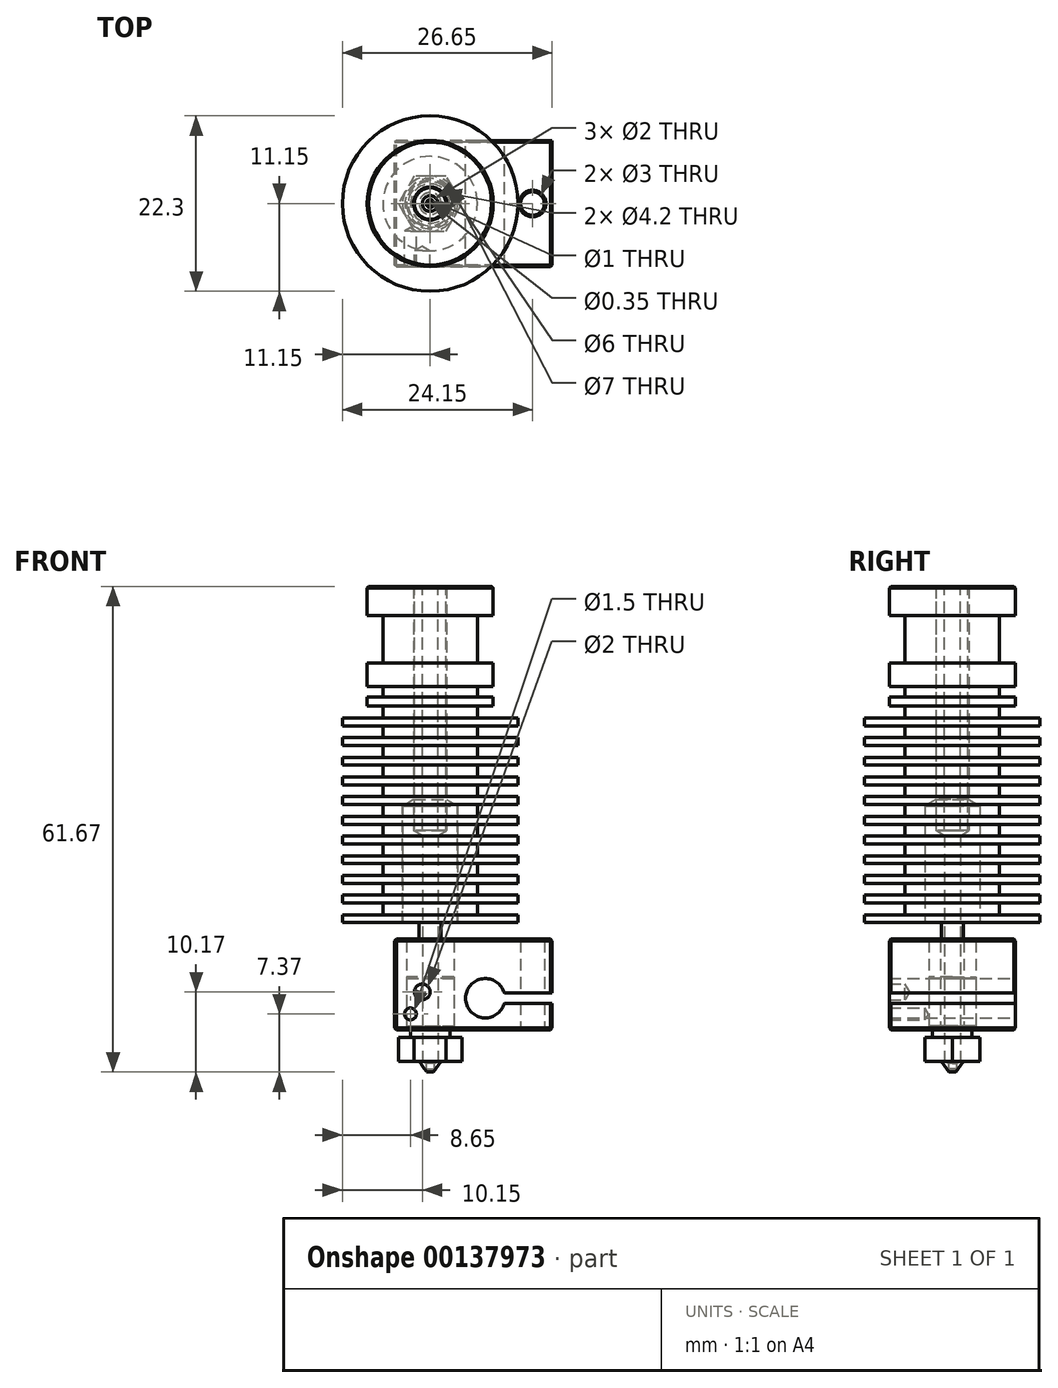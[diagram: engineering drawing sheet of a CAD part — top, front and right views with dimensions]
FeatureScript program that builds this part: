
annotation { "Feature Type Name" : "Feature", "Feature Type Description" : "" }
export const myFeature = defineFeature(function(context is Context, id is Id, definition is map)
    precondition{}
    {
        {
            assignVariable(context, id + "F0", {"name" : "A", "anyValue" : 0.35});
        }
        {
            assignVariable(context, id + "F1", {"name" : "D", "anyValue" : 1});
        }
        {
            var Q0;
            Q0=qCreatedBy(makeId("Front.planeOp"),FACE);
            var sketch = newSketch(context, id + "F2", { "sketchPlane" : qUnion([Q0])});
            skLineSegment(sketch, "E0", {"start": v(0, 21.35) * mm, "end": v(8, 21.35) * mm});
            skLineSegment(sketch, "E1", {"start": v(8, 21.35) * mm, "end": v(8, 17.65) * mm});
            skLineSegment(sketch, "E2", {"start": v(8, 17.65) * mm, "end": v(6, 17.65) * mm});
            skLineSegment(sketch, "E3", {"start": v(6, 17.65) * mm, "end": v(6, 11.65) * mm});
            skLineSegment(sketch, "E4", {"start": v(6, 11.65) * mm, "end": v(8, 11.65) * mm});
            skLineSegment(sketch, "E5", {"start": v(8, 11.65) * mm, "end": v(8, 8.65) * mm});
            skLineSegment(sketch, "E6", {"start": v(8, 8.65) * mm, "end": v(6, 8.65) * mm});
            skLineSegment(sketch, "E7", {"start": v(6, 8.65) * mm, "end": v(6, 7.3) * mm});
            skLineSegment(sketch, "E8", {"start": v(6, 7.3) * mm, "end": v(8, 7.3) * mm});
            skLineSegment(sketch, "E9", {"start": v(8, 7.3) * mm, "end": v(8, 6.15) * mm});
            skLineSegment(sketch, "E10", {"start": v(8, 6.15) * mm, "end": v(6, 6.15) * mm});
            skLineSegment(sketch, "E11", {"start": v(6, 6.15) * mm, "end": v(6, 4.65) * mm});
            skLineSegment(sketch, "E12", {"start": v(6, 4.65) * mm, "end": v(11.15, 4.65) * mm});
            skLineSegment(sketch, "E13", {"start": v(11.15, 4.65) * mm, "end": v(11.15, 3.65) * mm});
            skLineSegment(sketch, "E14", {"start": v(11.15, 3.65) * mm, "end": v(6, 3.65) * mm});
            skLineSegment(sketch, "E15.0.1.0", {"start": v(6, 3.65) * mm, "end": v(6, 2.15) * mm});
            skLineSegment(sketch, "E15.0.1.1", {"start": v(6, 2.15) * mm, "end": v(11.15, 2.15) * mm});
            skLineSegment(sketch, "E15.0.1.2", {"start": v(11.15, 2.15) * mm, "end": v(11.15, 1.15) * mm});
            skLineSegment(sketch, "E15.0.1.3", {"start": v(11.15, 1.15) * mm, "end": v(6, 1.15) * mm});
            skLineSegment(sketch, "E15.0.2.0", {"start": v(6, 1.15) * mm, "end": v(6, -0.35) * mm});
            skLineSegment(sketch, "E15.0.2.1", {"start": v(6, -0.35) * mm, "end": v(11.15, -0.35) * mm});
            skLineSegment(sketch, "E15.0.2.2", {"start": v(11.15, -0.35) * mm, "end": v(11.15, -1.35) * mm});
            skLineSegment(sketch, "E15.0.2.3", {"start": v(11.15, -1.35) * mm, "end": v(6, -1.35) * mm});
            skLineSegment(sketch, "E15.0.3.0", {"start": v(6, -1.35) * mm, "end": v(6, -2.85) * mm});
            skLineSegment(sketch, "E15.0.3.1", {"start": v(6, -2.85) * mm, "end": v(11.15, -2.85) * mm});
            skLineSegment(sketch, "E15.0.3.2", {"start": v(11.15, -2.85) * mm, "end": v(11.15, -3.85) * mm});
            skLineSegment(sketch, "E15.0.3.3", {"start": v(11.15, -3.85) * mm, "end": v(6, -3.85) * mm});
            skLineSegment(sketch, "E15.0.4.0", {"start": v(6, -3.85) * mm, "end": v(6, -5.35) * mm});
            skLineSegment(sketch, "E15.0.4.1", {"start": v(6, -5.35) * mm, "end": v(11.15, -5.35) * mm});
            skLineSegment(sketch, "E15.0.4.2", {"start": v(11.15, -5.35) * mm, "end": v(11.15, -6.35) * mm});
            skLineSegment(sketch, "E15.0.4.3", {"start": v(11.15, -6.35) * mm, "end": v(6, -6.35) * mm});
            skLineSegment(sketch, "E15.0.5.0", {"start": v(6, -6.35) * mm, "end": v(6, -7.85) * mm});
            skLineSegment(sketch, "E15.0.5.1", {"start": v(6, -7.85) * mm, "end": v(11.15, -7.85) * mm});
            skLineSegment(sketch, "E15.0.5.2", {"start": v(11.15, -7.85) * mm, "end": v(11.15, -8.85) * mm});
            skLineSegment(sketch, "E15.0.5.3", {"start": v(11.15, -8.85) * mm, "end": v(6, -8.85) * mm});
            skLineSegment(sketch, "E15.0.6.0", {"start": v(6, -8.85) * mm, "end": v(6, -10.35) * mm});
            skLineSegment(sketch, "E15.0.6.1", {"start": v(6, -10.35) * mm, "end": v(11.15, -10.35) * mm});
            skLineSegment(sketch, "E15.0.6.2", {"start": v(11.15, -10.35) * mm, "end": v(11.15, -11.35) * mm});
            skLineSegment(sketch, "E15.0.6.3", {"start": v(11.15, -11.35) * mm, "end": v(6, -11.35) * mm});
            skLineSegment(sketch, "E15.0.7.0", {"start": v(6, -11.35) * mm, "end": v(6, -12.85) * mm});
            skLineSegment(sketch, "E15.0.7.1", {"start": v(6, -12.85) * mm, "end": v(11.15, -12.85) * mm});
            skLineSegment(sketch, "E15.0.7.2", {"start": v(11.15, -12.85) * mm, "end": v(11.15, -13.85) * mm});
            skLineSegment(sketch, "E15.0.7.3", {"start": v(11.15, -13.85) * mm, "end": v(6, -13.85) * mm});
            skLineSegment(sketch, "E15.0.8.0", {"start": v(6, -13.85) * mm, "end": v(6, -15.35) * mm});
            skLineSegment(sketch, "E15.0.8.1", {"start": v(6, -15.35) * mm, "end": v(11.15, -15.35) * mm});
            skLineSegment(sketch, "E15.0.8.2", {"start": v(11.15, -15.35) * mm, "end": v(11.15, -16.35) * mm});
            skLineSegment(sketch, "E15.0.8.3", {"start": v(11.15, -16.35) * mm, "end": v(6, -16.35) * mm});
            skLineSegment(sketch, "E15.0.9.0", {"start": v(6, -16.35) * mm, "end": v(6, -17.85) * mm});
            skLineSegment(sketch, "E15.0.9.1", {"start": v(6, -17.85) * mm, "end": v(11.15, -17.85) * mm});
            skLineSegment(sketch, "E15.0.9.2", {"start": v(11.15, -17.85) * mm, "end": v(11.15, -18.85) * mm});
            skLineSegment(sketch, "E15.0.9.3", {"start": v(11.15, -18.85) * mm, "end": v(6, -18.85) * mm});
            skLineSegment(sketch, "E15.direction1", {"start": v(6, 3.65) * mm, "end": v(31, 3.65) * mm, "construction": true});
            skLineSegment(sketch, "E15.direction2", {"start": v(6, 3.65) * mm, "end": v(6, 1.15) * mm, "construction": true});
            skLineSegment(sketch, "E16", {"start": v(6, -18.85) * mm, "end": v(6, -20.35) * mm});
            skLineSegment(sketch, "E17", {"start": v(6, -20.35) * mm, "end": v(11.15, -20.35) * mm});
            skLineSegment(sketch, "E18", {"start": v(11.15, -20.35) * mm, "end": v(11.15, -21.35) * mm});
            skLineSegment(sketch, "E19", {"start": v(11.15, -21.35) * mm, "end": v(0, -21.35) * mm});
            skLineSegment(sketch, "E20", {"start": v(0, 21.35) * mm, "end": v(0, -21.35) * mm});
            skPoint(sketch, "E21.orphan", {"position": v(6, -21.35) * mm});
            skSolve(sketch);
        }
        {
            var Q0;
            Q0=makeQuery(id+"F2.imprint","IMPRINT",FACE,{"disambiguationData":[TD([[makeQuery(id+"F2.imprint","IMPRINT",EDGE,{"derivedFrom":sQuery(id+"F2.wireOp",EDGE,"E0")}),-1.0]])]});
            var Q1;
            Q1=sQuery(id+"F2.wireOp",EDGE,"E20");
            revolve(context, id + "F3", {"entities" : qUnion([Q0]), "axis" : qUnion([Q1]), "revolveType" : RevolveType.FULL});
        }
        {
            var Q0;
            Q0=makeQuery(id+"F3.opRevolve","SWEPT_FACE",FACE,{"disambiguationData":[OSD([sQuery(id+"F2.wireOp",EDGE,"E19")])]});
            var sketch = newSketch(context, id + "F4", { "sketchPlane" : qUnion([Q0])});
            skPoint(sketch, "E22", {"position": v(0, 0) * mm});
            skSolve(sketch);
        }
        {
            var Q0;
            Q0=sQuery(id+"F4.wireOp",VERTEX,"E22");
            var Q1;
            Q1=makeQuery(id+"F3.opRevolve","SWEPT_BODY",BODY,{"disambiguationData":[OSD([sQuery(id+"F2.wireOp",EDGE,"E0"),sQuery(id+"F2.wireOp",EDGE,"E1"),sQuery(id+"F2.wireOp",EDGE,"E2"),sQuery(id+"F2.wireOp",EDGE,"E3"),sQuery(id+"F2.wireOp",EDGE,"E4"),sQuery(id+"F2.wireOp",EDGE,"E5"),sQuery(id+"F2.wireOp",EDGE,"E6"),sQuery(id+"F2.wireOp",EDGE,"E7"),sQuery(id+"F2.wireOp",EDGE,"E8"),sQuery(id+"F2.wireOp",EDGE,"E9"),sQuery(id+"F2.wireOp",EDGE,"E10"),sQuery(id+"F2.wireOp",EDGE,"E11"),sQuery(id+"F2.wireOp",EDGE,"E12"),sQuery(id+"F2.wireOp",EDGE,"E13"),sQuery(id+"F2.wireOp",EDGE,"E14"),sQuery(id+"F2.wireOp",EDGE,"E15.0.1.0"),sQuery(id+"F2.wireOp",EDGE,"E15.0.1.1"),sQuery(id+"F2.wireOp",EDGE,"E15.0.1.2"),sQuery(id+"F2.wireOp",EDGE,"E15.0.1.3"),sQuery(id+"F2.wireOp",EDGE,"E15.0.2.0"),sQuery(id+"F2.wireOp",EDGE,"E15.0.2.1"),sQuery(id+"F2.wireOp",EDGE,"E15.0.2.2"),sQuery(id+"F2.wireOp",EDGE,"E15.0.2.3"),sQuery(id+"F2.wireOp",EDGE,"E15.0.3.0"),sQuery(id+"F2.wireOp",EDGE,"E15.0.3.1"),sQuery(id+"F2.wireOp",EDGE,"E15.0.3.2"),sQuery(id+"F2.wireOp",EDGE,"E15.0.3.3"),sQuery(id+"F2.wireOp",EDGE,"E15.0.4.0"),sQuery(id+"F2.wireOp",EDGE,"E15.0.4.1"),sQuery(id+"F2.wireOp",EDGE,"E15.0.4.2"),sQuery(id+"F2.wireOp",EDGE,"E15.0.4.3"),sQuery(id+"F2.wireOp",EDGE,"E15.0.5.0"),sQuery(id+"F2.wireOp",EDGE,"E15.0.5.1"),sQuery(id+"F2.wireOp",EDGE,"E15.0.5.2"),sQuery(id+"F2.wireOp",EDGE,"E15.0.5.3"),sQuery(id+"F2.wireOp",EDGE,"E15.0.6.0"),sQuery(id+"F2.wireOp",EDGE,"E15.0.6.1"),sQuery(id+"F2.wireOp",EDGE,"E15.0.6.2"),sQuery(id+"F2.wireOp",EDGE,"E15.0.6.3"),sQuery(id+"F2.wireOp",EDGE,"E15.0.7.0"),sQuery(id+"F2.wireOp",EDGE,"E15.0.7.1"),sQuery(id+"F2.wireOp",EDGE,"E15.0.7.2"),sQuery(id+"F2.wireOp",EDGE,"E15.0.7.3"),sQuery(id+"F2.wireOp",EDGE,"E15.0.8.0"),sQuery(id+"F2.wireOp",EDGE,"E15.0.8.1"),sQuery(id+"F2.wireOp",EDGE,"E15.0.8.2"),sQuery(id+"F2.wireOp",EDGE,"E15.0.8.3"),sQuery(id+"F2.wireOp",EDGE,"E15.0.9.0"),sQuery(id+"F2.wireOp",EDGE,"E15.0.9.1"),sQuery(id+"F2.wireOp",EDGE,"E15.0.9.2"),sQuery(id+"F2.wireOp",EDGE,"E15.0.9.3"),sQuery(id+"F2.wireOp",EDGE,"E16"),sQuery(id+"F2.wireOp",EDGE,"E17"),sQuery(id+"F2.wireOp",EDGE,"E18"),sQuery(id+"F2.wireOp",EDGE,"E19"),sQuery(id+"F2.wireOp",EDGE,"E20")])]});
            hole(context, id + "F5", {"style" : HoleStyle.SIMPLE, "endStyle" : HoleEndStyle.BLIND, "holeDiameter" : 7 * mm, "holeDepth" : 14.8 * mm, "locations" : qUnion([Q0]), "scope" : qUnion([Q1])});
        }
        {
            var Q0;
            Q0=qCreatedBy(makeId("Front.planeOp"),FACE);
            var sketch = newSketch(context, id + "F6", { "sketchPlane" : qUnion([Q0])});
            skLineSegment(sketch, "E23", {"start": v(0, -6.55) * mm, "end": v(3.5, -6.55) * mm});
            skLineSegment(sketch, "E24", {"start": v(3.5, -6.55) * mm, "end": v(3.5, -21.35) * mm});
            skLineSegment(sketch, "E25", {"start": v(3.5, -21.35) * mm, "end": v(1.4, -21.35) * mm});
            skLineSegment(sketch, "E26", {"start": v(1.4, -21.35) * mm, "end": v(1.4, -23.45) * mm});
            skLineSegment(sketch, "E27", {"start": v(1.4, -23.45) * mm, "end": v(3, -23.45) * mm});
            skLineSegment(sketch, "E28", {"start": v(3, -23.45) * mm, "end": v(3, -28.45) * mm});
            skLineSegment(sketch, "E29", {"start": v(3, -28.45) * mm, "end": v(0, -28.45) * mm});
            skLineSegment(sketch, "E30", {"start": v(0, -28.45) * mm, "end": v(0, -6.55) * mm});
            skLineSegment(sketch, "E31.0", {"start": v(3.5, -21.35) * mm, "end": v(-3.5, -21.35) * mm, "construction": true});
            skSolve(sketch);
        }
        {
            var Q0;
            Q0=qSketchRegion(id+"F6",true);
            var Q1;
            Q1=sQuery(id+"F6.wireOp",EDGE,"E30");
            revolve(context, id + "F7", {"entities" : qUnion([Q0]), "axis" : qUnion([Q1]), "revolveType" : RevolveType.FULL});
        }
        {
            var Q0;
            Q0=makeQuery(id+"F7.opRevolve","SWEPT_FACE",FACE,{"disambiguationData":[OSD([sQuery(id+"F6.wireOp",EDGE,"E23")])]});
            var sketch = newSketch(context, id + "F8", { "sketchPlane" : qUnion([Q0])});
            skPoint(sketch, "E32", {"position": v(0, 0) * mm});
            skSolve(sketch);
        }
        {
            var Q0;
            Q0=sQuery(id+"F8.wireOp",VERTEX,"E32");
            var Q1;
            Q1=makeQuery(id+"F7.opRevolve","SWEPT_BODY",BODY,{"disambiguationData":[OSD([sQuery(id+"F6.wireOp",EDGE,"E23"),sQuery(id+"F6.wireOp",EDGE,"E24"),sQuery(id+"F6.wireOp",EDGE,"E25"),sQuery(id+"F6.wireOp",EDGE,"E26"),sQuery(id+"F6.wireOp",EDGE,"E27"),sQuery(id+"F6.wireOp",EDGE,"E28"),sQuery(id+"F6.wireOp",EDGE,"E29"),sQuery(id+"F6.wireOp",EDGE,"E30")])]});
            hole(context, id + "F9", {"style" : HoleStyle.SIMPLE, "endStyle" : HoleEndStyle.THROUGH, "holeDiameter" : 2 * mm, "locations" : qUnion([Q0]), "scope" : qUnion([Q1]), "isTappedThrough" : true});
        }
        {
            var Q0;
            Q0=makeQuery(id+"F3.opRevolve","SWEPT_FACE",FACE,{"disambiguationData":[OSD([sQuery(id+"F2.wireOp",EDGE,"E0")])]});
            var sketch = newSketch(context, id + "F10", { "sketchPlane" : qUnion([Q0])});
            skPoint(sketch, "E33", {"position": v(0, 0) * mm});
            skSolve(sketch);
        }
        {
            var Q0;
            Q0=sQuery(id+"F10.wireOp",VERTEX,"E33");
            var Q1;
            Q1=makeQuery(id+"F3.opRevolve","SWEPT_BODY",BODY,{"disambiguationData":[OSD([sQuery(id+"F2.wireOp",EDGE,"E0"),sQuery(id+"F2.wireOp",EDGE,"E1"),sQuery(id+"F2.wireOp",EDGE,"E2"),sQuery(id+"F2.wireOp",EDGE,"E3"),sQuery(id+"F2.wireOp",EDGE,"E4"),sQuery(id+"F2.wireOp",EDGE,"E5"),sQuery(id+"F2.wireOp",EDGE,"E6"),sQuery(id+"F2.wireOp",EDGE,"E7"),sQuery(id+"F2.wireOp",EDGE,"E8"),sQuery(id+"F2.wireOp",EDGE,"E9"),sQuery(id+"F2.wireOp",EDGE,"E10"),sQuery(id+"F2.wireOp",EDGE,"E11"),sQuery(id+"F2.wireOp",EDGE,"E12"),sQuery(id+"F2.wireOp",EDGE,"E13"),sQuery(id+"F2.wireOp",EDGE,"E14"),sQuery(id+"F2.wireOp",EDGE,"E15.0.1.0"),sQuery(id+"F2.wireOp",EDGE,"E15.0.1.1"),sQuery(id+"F2.wireOp",EDGE,"E15.0.1.2"),sQuery(id+"F2.wireOp",EDGE,"E15.0.1.3"),sQuery(id+"F2.wireOp",EDGE,"E15.0.2.0"),sQuery(id+"F2.wireOp",EDGE,"E15.0.2.1"),sQuery(id+"F2.wireOp",EDGE,"E15.0.2.2"),sQuery(id+"F2.wireOp",EDGE,"E15.0.2.3"),sQuery(id+"F2.wireOp",EDGE,"E15.0.3.0"),sQuery(id+"F2.wireOp",EDGE,"E15.0.3.1"),sQuery(id+"F2.wireOp",EDGE,"E15.0.3.2"),sQuery(id+"F2.wireOp",EDGE,"E15.0.3.3"),sQuery(id+"F2.wireOp",EDGE,"E15.0.4.0"),sQuery(id+"F2.wireOp",EDGE,"E15.0.4.1"),sQuery(id+"F2.wireOp",EDGE,"E15.0.4.2"),sQuery(id+"F2.wireOp",EDGE,"E15.0.4.3"),sQuery(id+"F2.wireOp",EDGE,"E15.0.5.0"),sQuery(id+"F2.wireOp",EDGE,"E15.0.5.1"),sQuery(id+"F2.wireOp",EDGE,"E15.0.5.2"),sQuery(id+"F2.wireOp",EDGE,"E15.0.5.3"),sQuery(id+"F2.wireOp",EDGE,"E15.0.6.0"),sQuery(id+"F2.wireOp",EDGE,"E15.0.6.1"),sQuery(id+"F2.wireOp",EDGE,"E15.0.6.2"),sQuery(id+"F2.wireOp",EDGE,"E15.0.6.3"),sQuery(id+"F2.wireOp",EDGE,"E15.0.7.0"),sQuery(id+"F2.wireOp",EDGE,"E15.0.7.1"),sQuery(id+"F2.wireOp",EDGE,"E15.0.7.2"),sQuery(id+"F2.wireOp",EDGE,"E15.0.7.3"),sQuery(id+"F2.wireOp",EDGE,"E15.0.8.0"),sQuery(id+"F2.wireOp",EDGE,"E15.0.8.1"),sQuery(id+"F2.wireOp",EDGE,"E15.0.8.2"),sQuery(id+"F2.wireOp",EDGE,"E15.0.8.3"),sQuery(id+"F2.wireOp",EDGE,"E15.0.9.0"),sQuery(id+"F2.wireOp",EDGE,"E15.0.9.1"),sQuery(id+"F2.wireOp",EDGE,"E15.0.9.2"),sQuery(id+"F2.wireOp",EDGE,"E15.0.9.3"),sQuery(id+"F2.wireOp",EDGE,"E16"),sQuery(id+"F2.wireOp",EDGE,"E17"),sQuery(id+"F2.wireOp",EDGE,"E18"),sQuery(id+"F2.wireOp",EDGE,"E19"),sQuery(id+"F2.wireOp",EDGE,"E20")])]});
            var Q2;
            Q2=makeQuery(id+"F7.opRevolve","SWEPT_BODY",BODY,{"disambiguationData":[OSD([sQuery(id+"F6.wireOp",EDGE,"E23"),sQuery(id+"F6.wireOp",EDGE,"E24"),sQuery(id+"F6.wireOp",EDGE,"E25"),sQuery(id+"F6.wireOp",EDGE,"E26"),sQuery(id+"F6.wireOp",EDGE,"E27"),sQuery(id+"F6.wireOp",EDGE,"E28"),sQuery(id+"F6.wireOp",EDGE,"E29"),sQuery(id+"F6.wireOp",EDGE,"E30")])]});
            hole(context, id + "F11", {"style" : HoleStyle.SIMPLE, "endStyle" : HoleEndStyle.BLIND, "holeDiameter" : 4.2 * mm, "holeDepth" : 31 * mm, "locations" : qUnion([Q0]), "scope" : qUnion([Q1, Q2])});
        }
        {
            var Q0;
            Q0=qCreatedBy(makeId("Front.planeOp"),FACE);
            var sketch = newSketch(context, id + "F12", { "sketchPlane" : qUnion([Q0])});
            skLineSegment(sketch, "E34.0", {"start": v(-2.1, -9.65) * mm, "end": v(2.1, -9.65) * mm, "construction": true});
            skLineSegment(sketch, "E35.bottom", {"start": v(1, 21.35) * mm, "end": v(2, 21.35) * mm});
            skLineSegment(sketch, "E35.top", {"start": v(1, -9.65) * mm, "end": v(2, -9.65) * mm});
            skLineSegment(sketch, "E35.left", {"start": v(1, 21.35) * mm, "end": v(1, -9.65) * mm});
            skLineSegment(sketch, "E35.right", {"start": v(2, 21.35) * mm, "end": v(2, -9.65) * mm});
            skLineSegment(sketch, "E36", {"start": v(0, 26.07) * mm, "end": v(0, -35.6) * mm, "construction": true});
            skLineSegment(sketch, "E37.0", {"start": v(-2.1, 21.35) * mm, "end": v(2.1, 21.35) * mm, "construction": true});
            skSolve(sketch);
        }
        {
            var Q0;
            Q0=qSketchRegion(id+"F12",true);
            var Q1;
            Q1=qConstructionFilter(qBodyType(qCreatedBy(id+"F12",EDGE),BodyType.WIRE),ConstructionObject.NO);
            var Q2;
            Q2=sQuery(id+"F12.wireOp",EDGE,"E36");
            revolve(context, id + "F13", {"entities" : qUnion([Q0]), "surfaceEntities" : qUnion([Q1]), "axis" : qUnion([Q2]), "revolveType" : RevolveType.FULL});
        }
        {
            var Q0;
            Q0=makeQuery(id+"F7.opRevolve","SWEPT_FACE",FACE,{"disambiguationData":[OSD([sQuery(id+"F6.wireOp",EDGE,"E27")])]});
            var sketch = newSketch(context, id + "F14", { "sketchPlane" : qUnion([Q0])});
            skLineSegment(sketch, "E38.bottom", {"start": v(-4.5, -8) * mm, "end": v(15.5, -8) * mm});
            skLineSegment(sketch, "E38.top", {"start": v(-4.5, 8) * mm, "end": v(15.5, 8) * mm});
            skLineSegment(sketch, "E38.left", {"start": v(-4.5, -8) * mm, "end": v(-4.5, 8) * mm});
            skLineSegment(sketch, "E38.right", {"start": v(15.5, -8) * mm, "end": v(15.5, 8) * mm});
            skPoint(sketch, "E39", {"position": v(0, 0) * mm});
            skPoint(sketch, "E40", {"position": v(13, 0) * mm});
            skSolve(sketch);
        }
        {
            var Q0;
            Q0=qSketchRegion(id+"F14",true);
            extrude(context, id + "F15", {"entities" : qUnion([Q0]), "oppositeDirection" : true, "depth" : 11.5 * mm});
        }
        {
            var Q0;
            Q0=sQuery(id+"F14.wireOp",VERTEX,"E39");
            var Q1;
            Q1=makeQuery(id+"F15.opExtrude","SWEPT_BODY",BODY,{"disambiguationData":[OSD([sQuery(id+"F14.wireOp",EDGE,"E38.bottom"),sQuery(id+"F14.wireOp",EDGE,"E38.top"),sQuery(id+"F14.wireOp",EDGE,"E38.left"),sQuery(id+"F14.wireOp",EDGE,"E38.right")])]});
            hole(context, id + "F16", {"style" : HoleStyle.SIMPLE, "endStyle" : HoleEndStyle.THROUGH, "holeDiameter" : 6 * mm, "locations" : qUnion([Q0]), "scope" : qUnion([Q1]), "isTappedThrough" : true});
        }
        {
            var Q0;
            Q0=sQuery(id+"F14.wireOp",VERTEX,"E40");
            var Q1;
            Q1=makeQuery(id+"F15.opExtrude","SWEPT_BODY",BODY,{"disambiguationData":[OSD([sQuery(id+"F14.wireOp",EDGE,"E38.bottom"),sQuery(id+"F14.wireOp",EDGE,"E38.top"),sQuery(id+"F14.wireOp",EDGE,"E38.left"),sQuery(id+"F14.wireOp",EDGE,"E38.right")])]});
            hole(context, id + "F17", {"style" : HoleStyle.SIMPLE, "endStyle" : HoleEndStyle.THROUGH, "holeDiameter" : 3 * mm, "locations" : qUnion([Q0]), "scope" : qUnion([Q1]), "isTappedThrough" : true});
        }
        {
            var Q0;
            Q0=makeQuery(id+"F15.opExtrude","SWEPT_FACE",FACE,{"disambiguationData":[OSD([sQuery(id+"F14.wireOp",EDGE,"E38.bottom")])]});
            var sketch = newSketch(context, id + "F18", { "sketchPlane" : qUnion([Q0])});
            skPoint(sketch, "E41", {"position": v(-1, -30.15) * mm});
            skPoint(sketch, "E42", {"position": v(-2.5, -32.95) * mm});
            skPoint(sketch, "E43", {"position": v(7, -30.95) * mm});
            skLineSegment(sketch, "E44.bottom", {"start": v(15.5, -30.3) * mm, "end": v(7, -30.3) * mm});
            skLineSegment(sketch, "E44.top", {"start": v(15.5, -31.6) * mm, "end": v(7, -31.6) * mm});
            skLineSegment(sketch, "E44.left", {"start": v(15.5, -30.3) * mm, "end": v(15.5, -31.6) * mm});
            skLineSegment(sketch, "E44.right", {"start": v(7, -30.3) * mm, "end": v(7, -31.6) * mm});
            skSolve(sketch);
        }
        {
            var Q0;
            Q0=sQuery(id+"F18.wireOp",VERTEX,"E42");
            var Q1;
            Q1=makeQuery(id+"F15.opExtrude","SWEPT_BODY",BODY,{"disambiguationData":[OSD([sQuery(id+"F14.wireOp",EDGE,"E38.bottom"),sQuery(id+"F14.wireOp",EDGE,"E38.top"),sQuery(id+"F14.wireOp",EDGE,"E38.left"),sQuery(id+"F14.wireOp",EDGE,"E38.right")])]});
            hole(context, id + "F19", {"style" : HoleStyle.SIMPLE, "endStyle" : HoleEndStyle.BLIND, "holeDiameter" : 1.5 * mm, "holeDepth" : 4.5 * mm, "locations" : qUnion([Q0]), "scope" : qUnion([Q1])});
        }
        {
            var Q0;
            Q0=sQuery(id+"F18.wireOp",VERTEX,"E41");
            var Q1;
            Q1=makeQuery(id+"F15.opExtrude","SWEPT_BODY",BODY,{"disambiguationData":[OSD([sQuery(id+"F14.wireOp",EDGE,"E38.bottom"),sQuery(id+"F14.wireOp",EDGE,"E38.top"),sQuery(id+"F14.wireOp",EDGE,"E38.left"),sQuery(id+"F14.wireOp",EDGE,"E38.right")])]});
            hole(context, id + "F20", {"style" : HoleStyle.SIMPLE, "endStyle" : HoleEndStyle.BLIND, "holeDiameter" : 2 * mm, "holeDepth" : 2 * mm, "locations" : qUnion([Q0]), "scope" : qUnion([Q1])});
        }
        {
            var Q0;
            Q0=sQuery(id+"F18.wireOp",VERTEX,"E43");
            var Q1;
            Q1=makeQuery(id+"F15.opExtrude","SWEPT_BODY",BODY,{"disambiguationData":[OSD([sQuery(id+"F14.wireOp",EDGE,"E38.bottom"),sQuery(id+"F14.wireOp",EDGE,"E38.top"),sQuery(id+"F14.wireOp",EDGE,"E38.left"),sQuery(id+"F14.wireOp",EDGE,"E38.right")])]});
            hole(context, id + "F21", {"style" : HoleStyle.SIMPLE, "endStyle" : HoleEndStyle.THROUGH, "holeDiameter" : 5 * mm, "locations" : qUnion([Q0]), "scope" : qUnion([Q1]), "isTappedThrough" : true});
        }
        {
            var Q0;
            Q0=makeQuery(id+"F18.imprint","IMPRINT",FACE,{"disambiguationData":[TD([[makeQuery(id+"F18.imprint","IMPRINT",EDGE,{"derivedFrom":sQuery(id+"F18.wireOp",EDGE,"E44.bottom")}),1.0]])]});
            var Q1;
            Q1=makeQuery(id+"F15.opExtrude","SWEPT_BODY",BODY,{"disambiguationData":[OSD([sQuery(id+"F14.wireOp",EDGE,"E38.bottom"),sQuery(id+"F14.wireOp",EDGE,"E38.top"),sQuery(id+"F14.wireOp",EDGE,"E38.left"),sQuery(id+"F14.wireOp",EDGE,"E38.right")])]});
            extrude(context, id + "F22", {"entities" : qUnion([Q0]), "operationType" : NewBodyOperationType.REMOVE, "endBound" : BoundingType.UP_TO_BODY, "oppositeDirection" : true, "endBoundEntityBody" : qUnion([Q1]), "depth" : 25 * mm});
        }
        {
            var Q0;
            Q0=makeQuery(id+"F3.opRevolve","SWEPT_EDGE",EDGE,{"disambiguationData":[OSD([sQuery(id+"F2.wireOp",EDGE,"E0"),sQuery(id+"F2.wireOp",EDGE,"E1")])]});
            var Q1;
            Q1=makeQuery(id+"F5.hole-0.boolean.opBoolean","COPY",EDGE,{"derivedFrom":makeQuery(id+"F5.hole-0.opRevolve","SWEPT_EDGE",EDGE,{"disambiguationData":[OSD([sQuery(id+"F5.hole-0.sketch.wireOp",EDGE,"core_line_2"),sQuery(id+"F5.hole-0.sketch.wireOp",EDGE,"core_line_3")])]})});
            var Q2;
            Q2=makeQuery(id+"F5.hole-0.boolean.opBoolean","COPY",EDGE,{"derivedFrom":makeQuery(id+"F5.hole-0.opRevolve","SWEPT_EDGE",EDGE,{"disambiguationData":[OSD([sQuery(id+"F5.hole-0.sketch.wireOp",EDGE,"core_line_1"),sQuery(id+"F5.hole-0.sketch.wireOp",EDGE,"core_line_2")])]})});
            var Q3;
            Q3=makeQuery(id+"F7.opRevolve","SWEPT_EDGE",EDGE,{"disambiguationData":[OSD([sQuery(id+"F6.wireOp",EDGE,"E27"),sQuery(id+"F6.wireOp",EDGE,"E28")])]});
            var Q4;
            Q4=makeQuery(id+"F7.opRevolve","SWEPT_EDGE",EDGE,{"disambiguationData":[OSD([sQuery(id+"F6.wireOp",EDGE,"E28"),sQuery(id+"F6.wireOp",EDGE,"E29")])]});
            var Q5;
            Q5=makeQuery(id+"F9.hole-0.boolean.opBoolean","INTERSECT",EDGE,{"derivedFrom":[makeQuery(id+"F7.opRevolve","SWEPT_FACE",FACE,{"disambiguationData":[OSD([sQuery(id+"F6.wireOp",EDGE,"E29")])]}),makeQuery(id+"F9.hole-0.opRevolve","SWEPT_FACE",FACE,{"disambiguationData":[OSD([sQuery(id+"F9.hole-0.sketch.wireOp",EDGE,"core_line_2")])]})]});
            var Q6;
            Q6=makeQuery(id+"F15.opExtrude","CAP_EDGE",EDGE,{"disambiguationData":[OSD([sQuery(id+"F14.wireOp",EDGE,"E38.left")])],"isStart":true});
            var Q7;
            Q7=makeQuery(id+"F15.opExtrude","CAP_EDGE",EDGE,{"disambiguationData":[OSD([sQuery(id+"F14.wireOp",EDGE,"E38.bottom")])],"isStart":true});
            var Q8;
            Q8=makeQuery(id+"F15.opExtrude","SWEPT_EDGE",EDGE,{"disambiguationData":[OSD([sQuery(id+"F14.wireOp",EDGE,"E38.bottom"),sQuery(id+"F14.wireOp",EDGE,"E38.left")])]});
            var Q9;
            {var subQ0=sQuery(id+"F14.wireOp",EDGE,"E38.bottom");var subQ1=sQuery(id+"F14.wireOp",EDGE,"E38.right");Q9=makeQuery(id+"F22.boolean.opBoolean","SPLIT",EDGE,{"disambiguationData":[TD([makeQuery(id+"F22.opExtrude","SWEPT_FACE",FACE,{"disambiguationData":[OSD([sQuery(id+"F18.wireOp",EDGE,"E44.bottom")])]})])],"derivedFrom":makeQuery(id+"F15.opExtrude","SWEPT_EDGE",EDGE,{"disambiguationData":[OSD([subQ0,subQ1])]})});}
            var Q10;
            {var subQ0=sQuery(id+"F14.wireOp",EDGE,"E38.right");var subQ1=sQuery(id+"F14.wireOp",EDGE,"E38.top");Q10=makeQuery(id+"F22.boolean.opBoolean","SPLIT",EDGE,{"disambiguationData":[TD([makeQuery(id+"F22.opExtrude","SWEPT_FACE",FACE,{"disambiguationData":[OSD([sQuery(id+"F18.wireOp",EDGE,"E44.bottom")])]})])],"derivedFrom":makeQuery(id+"F15.opExtrude","SWEPT_EDGE",EDGE,{"disambiguationData":[OSD([subQ1,subQ0])]})});}
            var Q11;
            Q11=makeQuery(id+"F15.opExtrude","CAP_EDGE",EDGE,{"disambiguationData":[OSD([sQuery(id+"F14.wireOp",EDGE,"E38.top")])],"isStart":true});
            var Q12;
            Q12=makeQuery(id+"F15.opExtrude","CAP_EDGE",EDGE,{"disambiguationData":[OSD([sQuery(id+"F14.wireOp",EDGE,"E38.right")])],"isStart":true});
            var Q13;
            Q13=makeQuery(id+"F15.opExtrude","CAP_EDGE",EDGE,{"disambiguationData":[OSD([sQuery(id+"F14.wireOp",EDGE,"E38.right")])],"isStart":false});
            var Q14;
            {var subQ0=sQuery(id+"F14.wireOp",EDGE,"E38.bottom");var subQ1=sQuery(id+"F14.wireOp",EDGE,"E38.right");Q14=makeQuery(id+"F22.boolean.opBoolean","SPLIT",EDGE,{"disambiguationData":[TD([makeQuery(id+"F22.opExtrude","SWEPT_FACE",FACE,{"disambiguationData":[OSD([sQuery(id+"F18.wireOp",EDGE,"E44.top")])]})])],"derivedFrom":makeQuery(id+"F15.opExtrude","SWEPT_EDGE",EDGE,{"disambiguationData":[OSD([subQ0,subQ1])]})});}
            var Q15;
            Q15=makeQuery(id+"F15.opExtrude","CAP_EDGE",EDGE,{"disambiguationData":[OSD([sQuery(id+"F14.wireOp",EDGE,"E38.bottom")])],"isStart":false});
            var Q16;
            Q16=makeQuery(id+"F15.opExtrude","SWEPT_EDGE",EDGE,{"disambiguationData":[OSD([sQuery(id+"F14.wireOp",EDGE,"E38.top"),sQuery(id+"F14.wireOp",EDGE,"E38.left")])]});
            var Q17;
            Q17=makeQuery(id+"F15.opExtrude","CAP_EDGE",EDGE,{"disambiguationData":[OSD([sQuery(id+"F14.wireOp",EDGE,"E38.top")])],"isStart":false});
            var Q18;
            Q18=makeQuery(id+"F15.opExtrude","CAP_EDGE",EDGE,{"disambiguationData":[OSD([sQuery(id+"F14.wireOp",EDGE,"E38.left")])],"isStart":false});
            var Q19;
            Q19=makeQuery(id+"F19.hole-0.boolean.opBoolean","COPY",EDGE,{"derivedFrom":makeQuery(id+"F19.hole-0.opRevolve","SWEPT_EDGE",EDGE,{"disambiguationData":[OSD([sQuery(id+"F19.hole-0.sketch.wireOp",EDGE,"core_line_2"),sQuery(id+"F19.hole-0.sketch.wireOp",EDGE,"core_line_3")])]})});
            var Q20;
            Q20=makeQuery(id+"F20.hole-0.boolean.opBoolean","COPY",FACE,{"derivedFrom":makeQuery(id+"F20.hole-0.opRevolve","SWEPT_FACE",FACE,{"disambiguationData":[OSD([sQuery(id+"F20.hole-0.sketch.wireOp",EDGE,"core_line_2")])]})});
            var Q21;
            Q21=makeQuery(id+"F21.hole-0.boolean.opBoolean","COPY",EDGE,{"derivedFrom":makeQuery(id+"F21.hole-0.opRevolve","SWEPT_EDGE",EDGE,{"disambiguationData":[OSD([sQuery(id+"F21.hole-0.sketch.wireOp",EDGE,"core_line_2"),sQuery(id+"F21.hole-0.sketch.wireOp",EDGE,"core_line_3")])]})});
            var Q22;
            Q22=makeQuery(id+"F17.hole-0.boolean.opBoolean","COPY",EDGE,{"derivedFrom":makeQuery(id+"F17.hole-0.opRevolve","SWEPT_EDGE",EDGE,{"disambiguationData":[OSD([sQuery(id+"F17.hole-0.sketch.wireOp",EDGE,"core_line_2"),sQuery(id+"F17.hole-0.sketch.wireOp",EDGE,"core_line_3")])]})});
            var Q23;
            Q23=makeQuery(id+"F15.opExtrude","CAP_FACE",FACE,{"disambiguationData":[OSD([sQuery(id+"F14.wireOp",EDGE,"E38.bottom"),sQuery(id+"F14.wireOp",EDGE,"E38.top"),sQuery(id+"F14.wireOp",EDGE,"E38.left"),sQuery(id+"F14.wireOp",EDGE,"E38.right")])],"isStart":true});
            var Q24;
            Q24=makeQuery(id+"F21.hole-0.boolean.opBoolean","INTERSECT",EDGE,{"derivedFrom":[makeQuery(id+"F15.opExtrude","SWEPT_FACE",FACE,{"disambiguationData":[OSD([sQuery(id+"F14.wireOp",EDGE,"E38.top")])]}),makeQuery(id+"F21.hole-0.opRevolve","SWEPT_FACE",FACE,{"disambiguationData":[OSD([sQuery(id+"F21.hole-0.sketch.wireOp",EDGE,"core_line_2")])]})]});
            var Q25;
            Q25=makeQuery(id+"F17.hole-0.boolean.opBoolean","INTERSECT",EDGE,{"derivedFrom":[makeQuery(id+"F15.opExtrude","CAP_FACE",FACE,{"disambiguationData":[OSD([sQuery(id+"F14.wireOp",EDGE,"E38.bottom"),sQuery(id+"F14.wireOp",EDGE,"E38.top"),sQuery(id+"F14.wireOp",EDGE,"E38.left"),sQuery(id+"F14.wireOp",EDGE,"E38.right")])],"isStart":false}),makeQuery(id+"F17.hole-0.opRevolve","SWEPT_FACE",FACE,{"disambiguationData":[OSD([sQuery(id+"F17.hole-0.sketch.wireOp",EDGE,"core_line_2")])]})]});
            var Q26;
            Q26=makeQuery(id+"F16.hole-0.boolean.opBoolean","INTERSECT",EDGE,{"derivedFrom":[makeQuery(id+"F15.opExtrude","CAP_FACE",FACE,{"disambiguationData":[OSD([sQuery(id+"F14.wireOp",EDGE,"E38.bottom"),sQuery(id+"F14.wireOp",EDGE,"E38.top"),sQuery(id+"F14.wireOp",EDGE,"E38.left"),sQuery(id+"F14.wireOp",EDGE,"E38.right")])],"isStart":false}),makeQuery(id+"F16.hole-0.opRevolve","SWEPT_FACE",FACE,{"disambiguationData":[OSD([sQuery(id+"F16.hole-0.sketch.wireOp",EDGE,"core_line_2")])]})]});
            var Q27;
            Q27=makeQuery(id+"F11.hole-0.boolean.opBoolean","COPY",EDGE,{"derivedFrom":makeQuery(id+"F11.hole-0.opRevolve","SWEPT_EDGE",EDGE,{"disambiguationData":[OSD([sQuery(id+"F11.hole-0.sketch.wireOp",EDGE,"core_line_2"),sQuery(id+"F11.hole-0.sketch.wireOp",EDGE,"core_line_3")])]})});
            chamfer(context, id + "F23", {"entities" : qUnion([Q0, Q1, Q2, Q3, Q4, Q5, Q6, Q7, Q8, Q9, Q10, Q11, Q12, Q13, Q14, Q15, Q16, Q17, Q18, Q19, Q20, Q21, Q22, Q23, Q24, Q25, Q26, Q27]), "width" : .2 * mm, "tangentPropagation" : true});
        }
        {
            var Q0;
            Q0=qCreatedBy(makeId("Front.planeOp"),FACE);
            var sketch = newSketch(context, id + "F24", { "sketchPlane" : qUnion([Q0])});
            skLineSegment(sketch, "E45", {"start": v(0, -28.45) * mm, "end": v(3, -28.45) * mm});
            skLineSegment(sketch, "E46", {"start": v(3, -28.45) * mm, "end": v(3, -34.45) * mm});
            skLineSegment(sketch, "E47", {"start": v(3, -34.45) * mm, "end": v(2.5, -34.45) * mm});
            skLineSegment(sketch, "E48", {"start": v(2.5, -34.45) * mm, "end": v(2.5, -38.95) * mm});
            skLineSegment(sketch, "E49", {"start": v(2.5, -38.95) * mm, "end": v(1.4, -38.95) * mm});
            skLineSegment(sketch, "E50", {"start": v(1.4, -38.95) * mm, "end": v(0, -40.95) * mm});
            skLineSegment(sketch, "E51", {"start": v(0, -40.95) * mm, "end": v(0, -28.45) * mm});
            skLineSegment(sketch, "E52.0", {"start": v(2.8, -28.45) * mm, "end": v(-2.8, -28.45) * mm, "construction": true});
            skLineSegment(sketch, "E53", {"start": v(0, -40.32) * mm, "end": v(0.44, -40.32) * mm});
            skSolve(sketch);
        }
        {
            var Q0;
            {var subQ2=sQuery(id+"F24.wireOp",EDGE,"E45");Q0=makeQuery(id+"F24.imprint","IMPRINT",FACE,{"disambiguationData":[TD([[makeQuery(id+"F24.imprint","IMPRINT",EDGE,{"derivedFrom":subQ2}),-1.0]])]});}
            var Q1;
            Q1=sQuery(id+"F24.wireOp",EDGE,"E51");
            revolve(context, id + "F25", {"entities" : qUnion([Q0]), "axis" : qUnion([Q1]), "revolveType" : RevolveType.FULL});
        }
        {
            var Q0;
            Q0=makeQuery(id+"F25.opRevolve","SWEPT_FACE",FACE,{"disambiguationData":[OSD([sQuery(id+"F24.wireOp",EDGE,"E49")])]});
            var sketch = newSketch(context, id + "F26", { "sketchPlane" : qUnion([Q0])});
            skCircle(sketch, "E54.cCircle", {"center": v(0, 0) * mm, "radius": 3.5 * mm, "construction": true});
            skLineSegment(sketch, "E54.0", {"start": v(-2.02, 3.5) * mm, "end": v(2.02, 3.5) * mm});
            skLineSegment(sketch, "E54.1", {"start": v(2.02, 3.5) * mm, "end": v(4.04, 0) * mm});
            skLineSegment(sketch, "E54.2", {"start": v(4.04, 0) * mm, "end": v(2.02, -3.5) * mm});
            skLineSegment(sketch, "E54.3", {"start": v(2.02, -3.5) * mm, "end": v(-2.02, -3.5) * mm});
            skLineSegment(sketch, "E54.4", {"start": v(-2.02, -3.5) * mm, "end": v(-4.04, 0) * mm});
            skLineSegment(sketch, "E54.5", {"start": v(-4.04, 0) * mm, "end": v(-2.02, 3.5) * mm});
            skPoint(sketch, "E54.0.midPoint", {"position": v(0, 3.5) * mm});
            skSolve(sketch);
        }
        {
            var Q0;
            Q0=qSketchRegion(id+"F26",true);
            extrude(context, id + "F27", {"entities" : qUnion([Q0]), "operationType" : NewBodyOperationType.ADD, "oppositeDirection" : true, "depth" : (10.5 - 7.5) * mm});
        }
        {
            var Q0;
            Q0=makeQuery(id+"F25.opRevolve","SWEPT_FACE",FACE,{"disambiguationData":[OSD([sQuery(id+"F24.wireOp",EDGE,"E45")])]});
            var sketch = newSketch(context, id + "F28", { "sketchPlane" : qUnion([Q0])});
            skPoint(sketch, "E55", {"position": v(0, 0) * mm});
            skSolve(sketch);
        }
        {
            var Q0;
            Q0=sQuery(id+"F28.wireOp",VERTEX,"E55");
            var Q1;
            Q1=makeQuery(id+"F25.opRevolve","SWEPT_BODY",BODY,{"disambiguationData":[OSD([sQuery(id+"F24.wireOp",EDGE,"E45"),sQuery(id+"F24.wireOp",EDGE,"E46"),sQuery(id+"F24.wireOp",EDGE,"E47"),sQuery(id+"F24.wireOp",EDGE,"E48"),sQuery(id+"F24.wireOp",EDGE,"E49"),sQuery(id+"F24.wireOp",EDGE,"E50"),sQuery(id+"F24.wireOp",EDGE,"E51")])]});
            hole(context, id + "F29", {"style" : HoleStyle.SIMPLE, "endStyle" : HoleEndStyle.BLIND, "holeDiameter" : 2 * mm, "holeDepth" : 10.5 * mm, "startFromSketch" : true, "locations" : qUnion([Q0]), "scope" : qUnion([Q1])});
        }
        {
            var Q0;
            Q0=sQuery(id+"F28.wireOp",VERTEX,"E55");
            var Q1;
            Q1=makeQuery(id+"F25.opRevolve","SWEPT_BODY",BODY,{"disambiguationData":[OSD([sQuery(id+"F24.wireOp",EDGE,"E45"),sQuery(id+"F24.wireOp",EDGE,"E46"),sQuery(id+"F24.wireOp",EDGE,"E47"),sQuery(id+"F24.wireOp",EDGE,"E48"),sQuery(id+"F24.wireOp",EDGE,"E49"),sQuery(id+"F24.wireOp",EDGE,"E50"),sQuery(id+"F24.wireOp",EDGE,"E51")])]});
            hole(context, id + "F30", {"style" : HoleStyle.SIMPLE, "endStyle" : HoleEndStyle.BLIND, "holeDiameter" : (getVariable(context, 'D')) * mm, "holeDepth" : 11.5 * mm, "startFromSketch" : true, "locations" : qUnion([Q0]), "scope" : qUnion([Q1])});
        }
        {
            var Q0;
            Q0=sQuery(id+"F28.wireOp",VERTEX,"E55");
            var Q1;
            Q1=makeQuery(id+"F25.opRevolve","SWEPT_BODY",BODY,{"disambiguationData":[OSD([sQuery(id+"F24.wireOp",EDGE,"E45"),sQuery(id+"F24.wireOp",EDGE,"E46"),sQuery(id+"F24.wireOp",EDGE,"E47"),sQuery(id+"F24.wireOp",EDGE,"E48"),sQuery(id+"F24.wireOp",EDGE,"E49"),sQuery(id+"F24.wireOp",EDGE,"E50"),sQuery(id+"F24.wireOp",EDGE,"E51"),sQuery(id+"F24.wireOp",EDGE,"E53")])]});
            hole(context, id + "F31", {"style" : HoleStyle.SIMPLE, "endStyle" : HoleEndStyle.THROUGH, "holeDiameter" : (getVariable(context, 'A')) * mm, "startFromSketch" : true, "locations" : qUnion([Q0]), "scope" : qUnion([Q1]), "isTappedThrough" : true});
        }
    });
